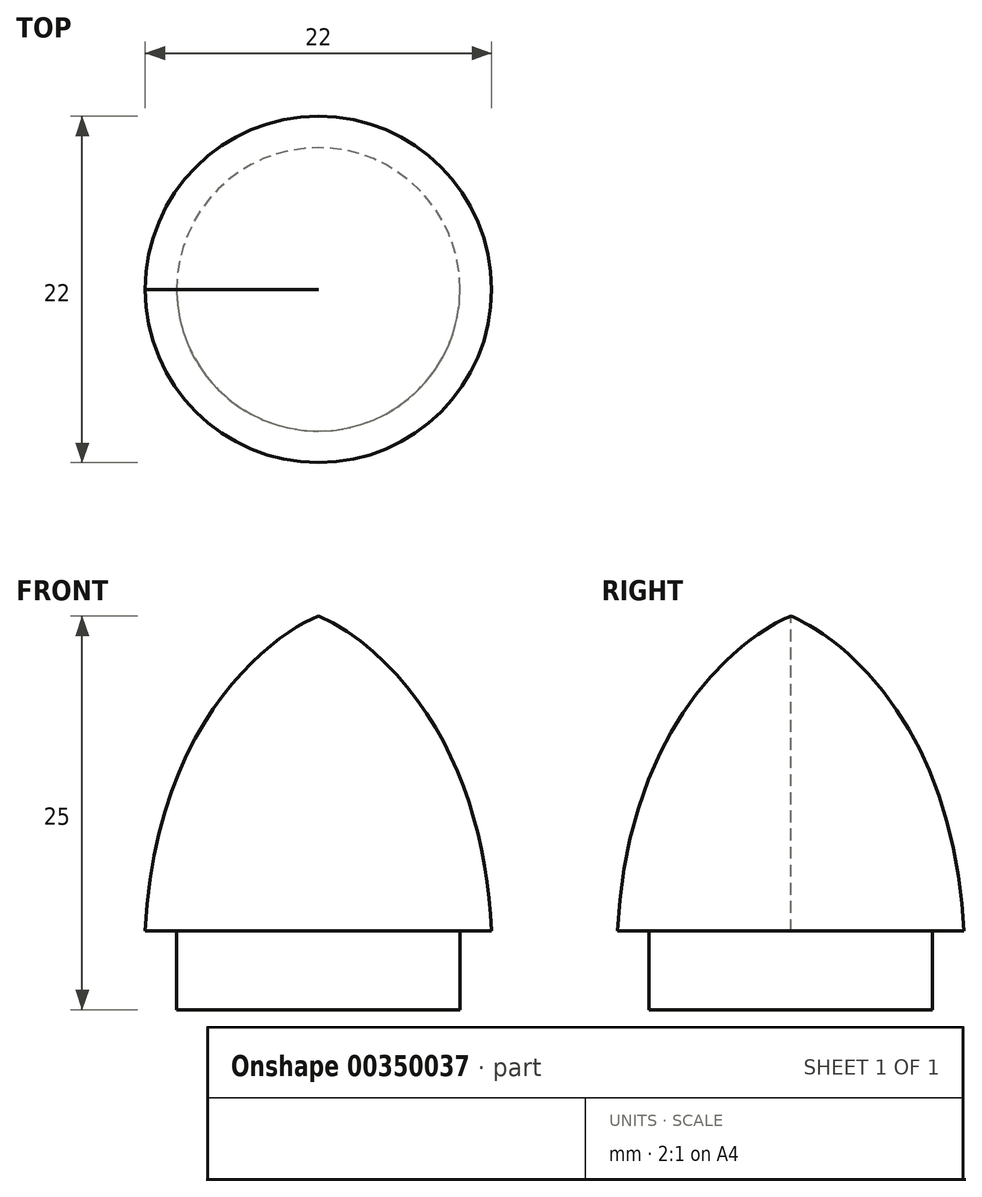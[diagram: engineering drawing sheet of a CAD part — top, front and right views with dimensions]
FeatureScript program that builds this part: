
annotation { "Feature Type Name" : "Feature", "Feature Type Description" : "" }
export const myFeature = defineFeature(function(context is Context, id is Id, definition is map)
    precondition{}
    {
        {
            var Q0;
            Q0=qCreatedBy(makeId("Top.planeOp"),FACE);
            var sketch = newSketch(context, id + "F0", { "sketchPlane" : qUnion([Q0])});
            skCircle(sketch, "E0", {"center": v(0, 0) * mm, "radius": 9 * mm});
            skCircle(sketch, "E1", {"center": v(0, 0) * mm, "radius": 11 * mm});
            skSolve(sketch);
        }
        {
            var Q0;
            Q0=qCreatedBy(makeId("Front.planeOp"),FACE);
            var sketch = newSketch(context, id + "F1", { "sketchPlane" : qUnion([Q0])});
            skLineSegment(sketch, "E2", {"start": v(0, 0) * mm, "end": v(-11, 0) * mm});
            skLineSegment(sketch, "E3", {"start": v(0, 0) * mm, "end": v(0, 20) * mm});
            skFitSpline(sketch, "E4", {"points": [v(-11, 0) * mm, v(0, 20) * mm], "startDerivative": vector(1.92, 39.77) * mm, "endDerivative": vector(9.02, 3.62) * mm});
            skSolve(sketch);
        }
        {
            var Q0;
            Q0=makeQuery(id+"F1.imprint","IMPRINT",FACE,{"disambiguationData":[TD([[makeQuery(id+"F1.imprint","IMPRINT",EDGE,{"derivedFrom":sQuery(id+"F1.wireOp",EDGE,"E2")}),-1.0]])]});
            var Q1;
            Q1=sQuery(id+"F1.wireOp",EDGE,"E3");
            revolve(context, id + "F2", {"entities" : qUnion([Q0]), "axis" : qUnion([Q1]), "revolveType" : RevolveType.FULL});
        }
        {
            var Q0;
            Q0=makeQuery(id+"F0.imprint","IMPRINT",FACE,{"disambiguationData":[TD([[makeQuery(id+"F0.imprint","IMPRINT",EDGE,{"derivedFrom":sQuery(id+"F0.wireOp",EDGE,"E0")}),1.0]])]});
            extrude(context, id + "F3", {"entities" : qUnion([Q0]), "operationType" : NewBodyOperationType.ADD, "oppositeDirection" : true, "depth" : 5 * mm});
        }
    });
